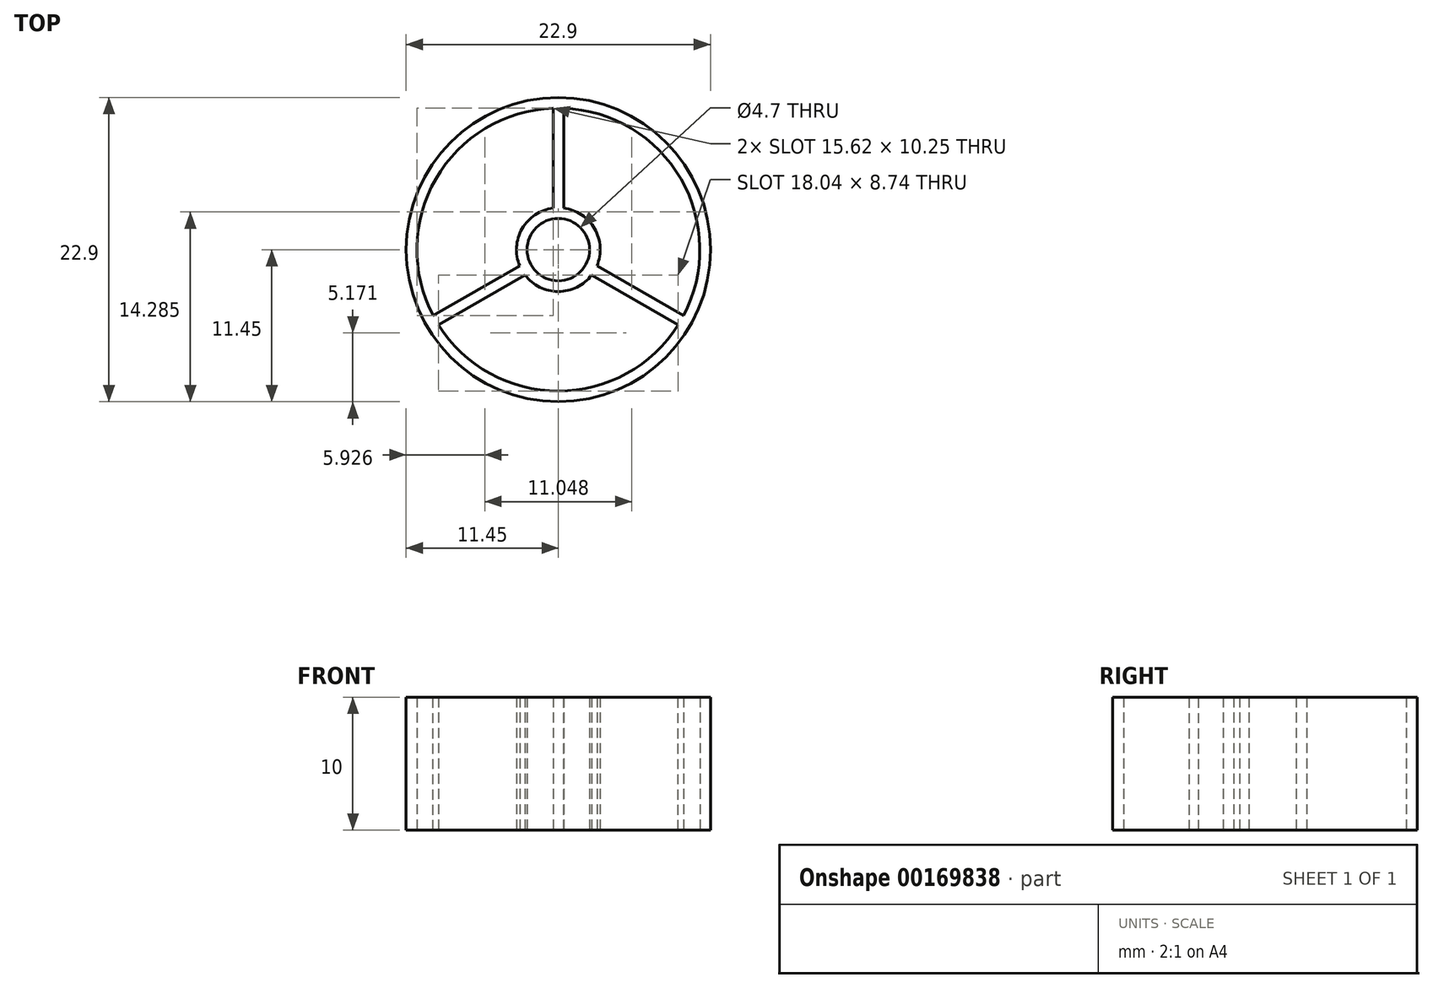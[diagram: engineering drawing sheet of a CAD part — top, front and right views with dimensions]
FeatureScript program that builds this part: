
annotation { "Feature Type Name" : "Feature", "Feature Type Description" : "" }
export const myFeature = defineFeature(function(context is Context, id is Id, definition is map)
    precondition{}
    {
        {
            var Q0;
            Q0=qCreatedBy(makeId("Front.planeOp"),FACE);
            var sketch = newSketch(context, id + "F0", { "sketchPlane" : qUnion([Q0])});
            skLineSegment(sketch, "E0.bottom", {"start": v(-11.45, 0) * mm, "end": v(-10.65, 0) * mm});
            skLineSegment(sketch, "E0.top", {"start": v(-11.45, 10) * mm, "end": v(-10.65, 10) * mm});
            skLineSegment(sketch, "E0.left", {"start": v(-11.45, 0) * mm, "end": v(-11.45, 10) * mm});
            skLineSegment(sketch, "E0.right", {"start": v(-10.65, 0) * mm, "end": v(-10.65, 10) * mm});
            skLineSegment(sketch, "E1.bottom", {"start": v(-3.15, 0) * mm, "end": v(-2.35, 0) * mm});
            skLineSegment(sketch, "E1.top", {"start": v(-3.15, 10) * mm, "end": v(-2.35, 10) * mm});
            skLineSegment(sketch, "E1.left", {"start": v(-3.15, 0) * mm, "end": v(-3.15, 10) * mm});
            skLineSegment(sketch, "E1.right", {"start": v(-2.35, 0) * mm, "end": v(-2.35, 10) * mm});
            skLineSegment(sketch, "E2", {"start": v(0, 0) * mm, "end": v(0, 10) * mm});
            skSolve(sketch);
        }
        {
            var Q0;
            Q0=qSketchRegion(id+"F0",true);
            var Q1;
            Q1=sQuery(id+"F0.wireOp",EDGE,"E2");
            revolve(context, id + "F1", {"entities" : qUnion([Q0]), "axis" : qUnion([Q1]), "revolveType" : RevolveType.FULL});
        }
        {
            var Q0;
            Q0=qCreatedBy(makeId("Top.planeOp"),FACE);
            var sketch = newSketch(context, id + "F2", { "sketchPlane" : qUnion([Q0])});
            skCircle(sketch, "E3.0", {"center": v(0, 0) * mm, "radius": 10.65 * mm, "construction": true});
            skCircle(sketch, "E4.0", {"center": v(0, 0) * mm, "radius": 2.35 * mm, "construction": true});
            skLineSegment(sketch, "E5.bottom", {"start": v(-0.4, 10.65) * mm, "end": v(0.4, 10.65) * mm});
            skLineSegment(sketch, "E5.top", {"start": v(-0.4, 2.35) * mm, "end": v(0.4, 2.35) * mm});
            skLineSegment(sketch, "E5.left", {"start": v(-0.4, 10.65) * mm, "end": v(-0.4, 2.35) * mm});
            skLineSegment(sketch, "E5.right", {"start": v(0.4, 10.65) * mm, "end": v(0.4, 2.35) * mm});
            skPoint(sketch, "E6", {"position": v(0, 2.35) * mm});
            skCircle(sketch, "E7.1.1", {"center": v(0, 0) * mm, "radius": 11.05 * mm, "construction": true});
            skCircle(sketch, "E7.2.1", {"center": v(0, 0) * mm, "radius": 11.05 * mm, "construction": true});
            skLineSegment(sketch, "E8.1.0", {"start": v(-1.84, -1.52) * mm, "end": v(-2.24, -0.83) * mm});
            skLineSegment(sketch, "E8.1.1", {"start": v(-9.02, -5.67) * mm, "end": v(-1.84, -1.52) * mm});
            skLineSegment(sketch, "E8.1.2", {"start": v(-9.42, -4.98) * mm, "end": v(-2.24, -0.83) * mm});
            skLineSegment(sketch, "E8.1.3", {"start": v(-9.02, -5.67) * mm, "end": v(-9.42, -4.98) * mm});
            skLineSegment(sketch, "E8.2.0", {"start": v(2.24, -0.83) * mm, "end": v(1.84, -1.52) * mm});
            skLineSegment(sketch, "E8.2.1", {"start": v(9.42, -4.98) * mm, "end": v(2.24, -0.83) * mm});
            skLineSegment(sketch, "E8.2.2", {"start": v(9.02, -5.67) * mm, "end": v(1.84, -1.52) * mm});
            skLineSegment(sketch, "E8.2.3", {"start": v(9.42, -4.98) * mm, "end": v(9.02, -5.67) * mm});
            skSolve(sketch);
        }
        {
            var Q0;
            Q0=qSketchRegion(id+"F2",true);
            var Q1;
            Q1=makeQuery(id+"F1.opRevolve","SWEPT_FACE",FACE,{"disambiguationData":[OSD([sQuery(id+"F0.wireOp",EDGE,"E1.top")])]});
            extrude(context, id + "F3", {"entities" : qUnion([Q0]), "operationType" : NewBodyOperationType.ADD, "endBound" : BoundingType.UP_TO_SURFACE, "endBoundEntityFace" : qUnion([Q1]), "depth" : 25 * mm});
        }
    });
